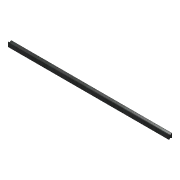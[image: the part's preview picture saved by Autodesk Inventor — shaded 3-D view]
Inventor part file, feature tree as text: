
AUTODESK INVENTOR PART (.ipt)
format: ipt  version: 2016 (Build 200138000, 138)  size: 78,336 bytes
history: native  units: mm
features: extrude x1, sketch x1
ambient origin geometry x8: Origin, YZ Plane, XZ Plane, XY Plane, X Axis, Y Axis, Z Axis, Center Point
bodies: Solid1 (feature_tree)
feature tree (2):
  extrude  "Extrusion1"  Depth=1.5mm
  sketch  "Sketch1"  dims[d9=1.5mm d10=1.5mm d11=753.25mm d12=0.0mm]
